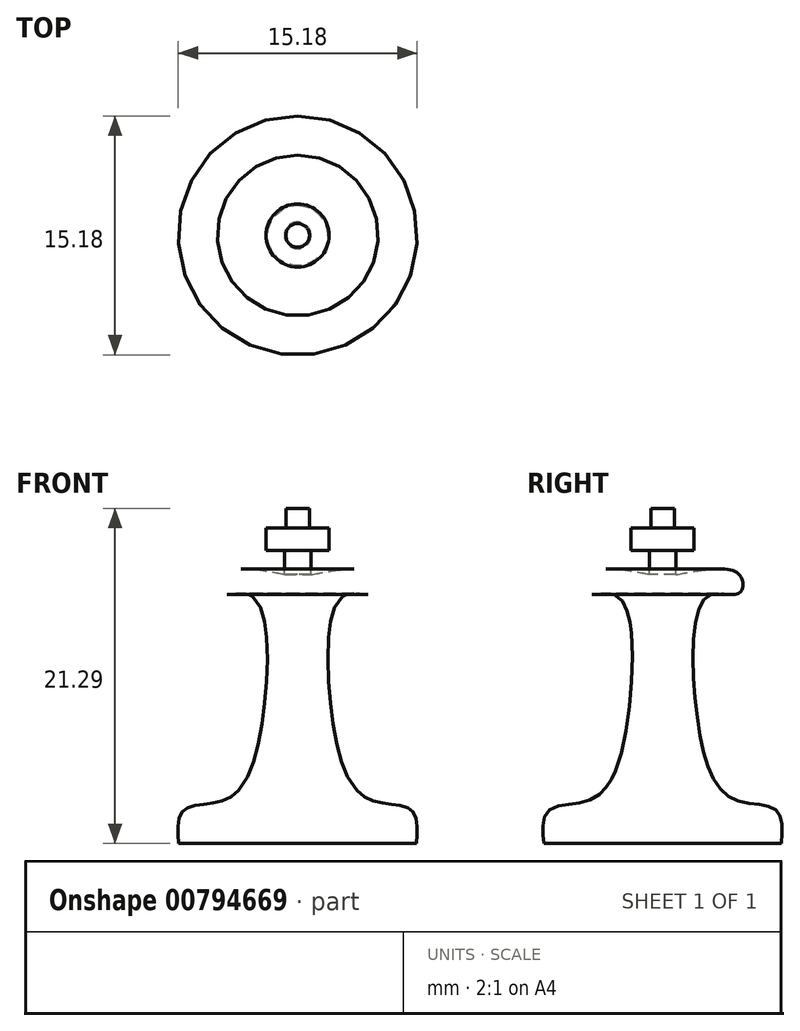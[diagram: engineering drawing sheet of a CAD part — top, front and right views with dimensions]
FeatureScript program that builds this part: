
annotation { "Feature Type Name" : "Feature", "Feature Type Description" : "" }
export const myFeature = defineFeature(function(context is Context, id is Id, definition is map)
    precondition{}
    {
        {
            var Q0;
            Q0=qCreatedBy(makeId("Top.planeOp"),FACE);
            var sketch = newSketch(context, id + "F0", { "sketchPlane" : qUnion([Q0])});
            skCircle(sketch, "E0", {"center": v(0, 0) * mm, "radius": 7.76 * mm});
            skSolve(sketch);
        }
        {
            var Q0;
            Q0=qCreatedBy(makeId("Right.planeOp"),FACE);
            var sketch = newSketch(context, id + "F1", { "sketchPlane" : qUnion([Q0])});
            skFitSpline(sketch, "E1", {"points": [v(7.55, 0) * mm, v(7.2, 2.15) * mm, v(4.42, 2.87) * mm, v(2.18, 8.14) * mm, v(2.9, 15.74) * mm, v(4.87, 15.92) * mm, v(4.87, 17.08) * mm, v(0.84, 17.08) * mm], "startDerivative": vector(1.7, 22.93) * mm, "endDerivative": vector(-32.86, -6.1) * mm});
            skLineSegment(sketch, "E2", {"start": v(0.84, 17.08) * mm, "end": v(0.84, 18.6) * mm});
            skLineSegment(sketch, "E3", {"start": v(0.84, 18.6) * mm, "end": v(2, 18.6) * mm});
            skLineSegment(sketch, "E4", {"start": v(2, 18.6) * mm, "end": v(2, 20.04) * mm});
            skLineSegment(sketch, "E5", {"start": v(2, 20.04) * mm, "end": v(0.75, 20.04) * mm});
            skLineSegment(sketch, "E6", {"start": v(0.75, 20.04) * mm, "end": v(0.75, 21.29) * mm});
            skLineSegment(sketch, "E7", {"start": v(0.75, 21.29) * mm, "end": v(0, 21.29) * mm});
            skLineSegment(sketch, "E8", {"start": v(0, 21.29) * mm, "end": v(0, 0) * mm});
            skLineSegment(sketch, "E9", {"start": v(0, 0) * mm, "end": v(7.55, 0) * mm});
            skSolve(sketch);
        }
        {
            var Q0;
            Q0=makeQuery(id+"F1.imprint","IMPRINT",FACE,{"disambiguationData":[TD([[makeQuery(id+"F1.imprint","IMPRINT",EDGE,{"derivedFrom":sQuery(id+"F1.wireOp",EDGE,"E1")}),1.0]])]});
            var Q1;
            Q1=sQuery(id+"F0.wireOp",EDGE,"E0");
            sweep(context, id + "F2", {"profiles" : qUnion([Q0]), "path" : qUnion([Q1])});
        }
    });
